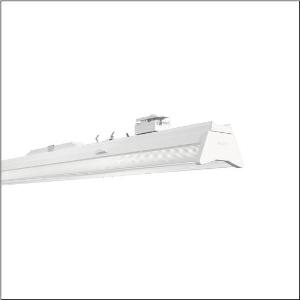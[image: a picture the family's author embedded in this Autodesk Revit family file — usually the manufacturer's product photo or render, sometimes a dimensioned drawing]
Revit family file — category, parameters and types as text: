
# Revit family: licross_r__21_performance_ho_52tm16cn4c5m_51b1
name_source: partatom
category: Lighting Fixtures
units: mm (PartAtom-declared; Revit-internal decimal feet)

## family parameters
Cut with Voids When Loaded = No
Host = Face
Light Source = No
Part Type = Normal
Room Calculation Point = No
Round Connector Dimension = Use Diameter
Shared = No

## types (1)
- --- (1 x LED, 12610 lm, 68.9 W, 4000K)
    Apparent Load = 69 VA
    CIE Flux Codes = 63 87 95 78 100
    Color Rendering = 80
    Color Temperature = 4000K
    Default Elevation = 1800 mm
    Description = Licross® 21 Performance HO, luminaire insert, of sheet steel, galvanised, coil coated, white, length: 1.500mm, width: 120mm, height: 123mm, LED rated luminous flux: 12.610lm, light colour: 840, control gear: ON/OFF Multilumen, CLOi, control gear: ECG Multilumen, with plug, 3-pole, with phase selection, mains connection: 220..240V, AC, 50/60Hz, start of lifetime: 69W, end of service life: 83W, halogen-free wiring, primary light control with lens, of plastic, primary optical cover: cover, of PMMA, light emission: direct/indirect distribution, primary light characteristic: symmetric, protection rating (complete): IP40, insulation class (complete): insulation class I (protective earthing), certification: CE, ENEC, UKCA, protection symbol: D if used in an environment without relevant dust loads with corresponding accessories, impact resistance: IK06, permissible ambient temperature for indoor applications: -35..+35°C, corresponds to IFS (International Featured Standards) requirements for safety and quality in the food industry, reducing of maximum allowable ambient temperature of 5°C with ceiling mounting, LABS conformity tested according to VDMA 24364:2018-05, packaging unit: 1 piece
    Height = 114 mm
    Lamp = 1 x LED
    Lamp Light Flux = 12610 lm
    Lamp Power = 68.9 W
    Lamp count = 1
    Length = 1500 mm
    Luminous efficacy = 183 lm/W
    Manufacturer = Siteco
    ModVariant = No
    Model = 52TM16CN4C5M
    Mounting Place = Ceiling
    Mounting Type = Pendant
    Number of Poles = 1
    OnlyDefault = Yes
    Power Factor = 1
    Product Name = Licross® 21 Performance HO
    Product group = luminaire insert
    ProductGroupID = 901
    Protection Class = Protection class I
    Protection Degree = IP 40
    RLX_Detail_Level = 1
    RLX_Emergency_Light_Flux = 0 lm
    RLX_Emergency_Type = 0
    RLX_Emergency_Type_DB = No
    RlxData = <blob elided: 31849 chars, md5=d913a691>
    Socket = socket
    Standby Power = 0 W
    System Light Flux = 12610 lm
    System Power = 69 W
    Type Comments = factory setting: luminous flux: 100 % | (A | C | E) | 162 mA
    Type Image = l_1256138.jpg
    URL = http://relux.com
    VarID = @adj_059871
    Voltage = 0 V
    Weight = 0.00 kg
    Width = 120 mm

## geometry (parser evidence)
native form markers: Blend x4, Sweep x11
no freeform markers — native parametric forms only
